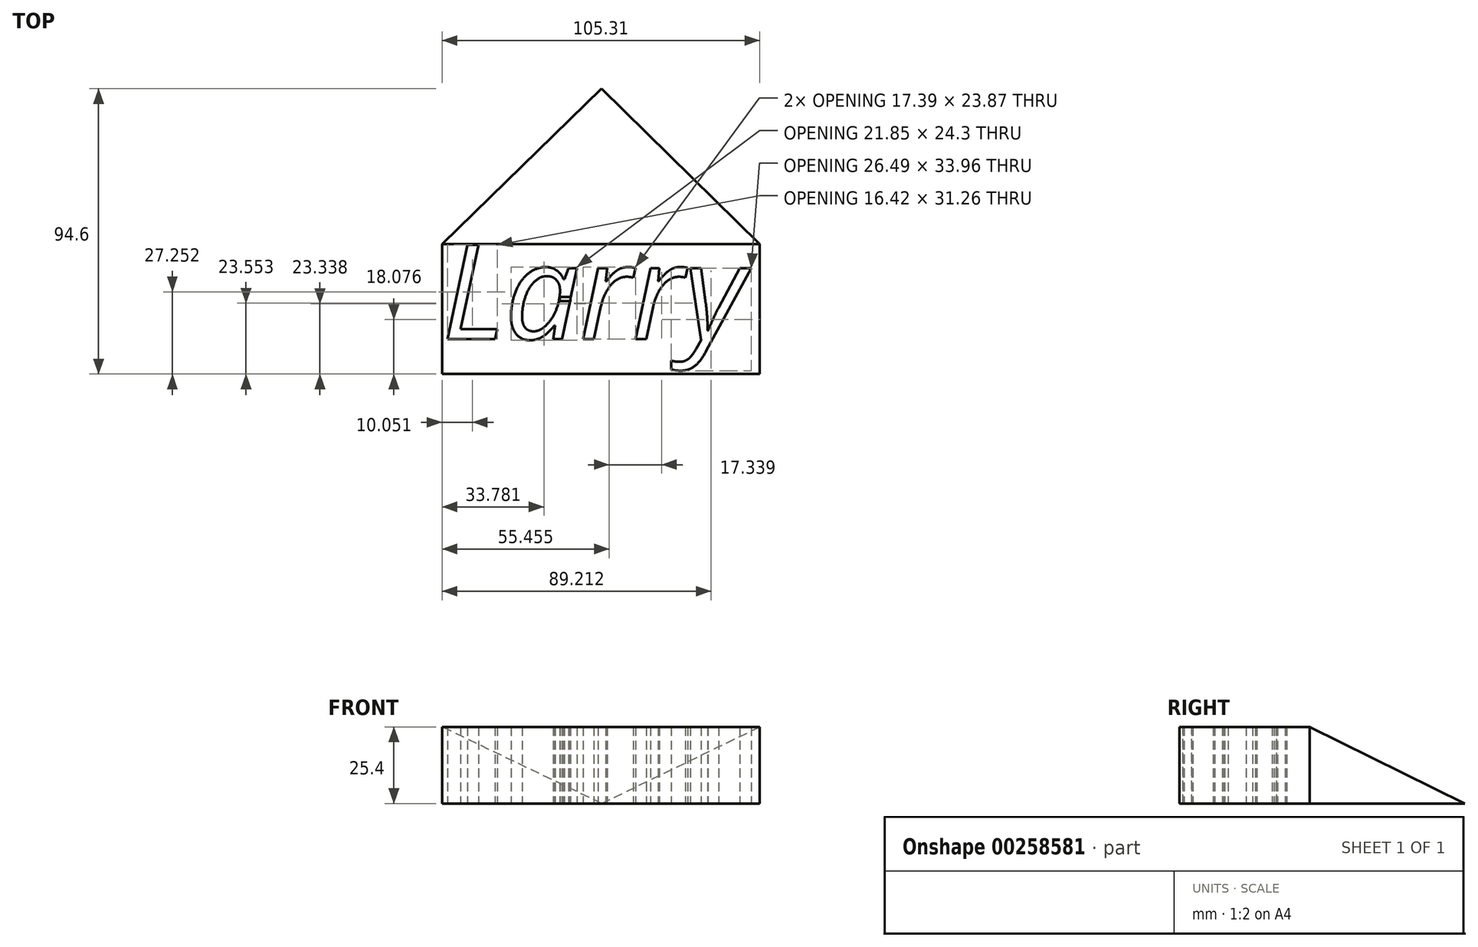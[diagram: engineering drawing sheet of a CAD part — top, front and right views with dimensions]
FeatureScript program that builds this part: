
annotation { "Feature Type Name" : "Feature", "Feature Type Description" : "" }
export const myFeature = defineFeature(function(context is Context, id is Id, definition is map)
    precondition{}
    {
        {
            var Q0;
            Q0=qCreatedBy(makeId("Top.planeOp"),FACE);
            var sketch = newSketch(context, id + "F0", { "sketchPlane" : qUnion([Q0])});
            skText(sketch, "E0", { "text": "Larry", "fontName": "OpenSans-Italic.ttf"});
            skLineSegment(sketch, "E1.bottom", {"start": v(-75.1, 0) * mm, "end": v(30.21, 0) * mm});
            skLineSegment(sketch, "E1.top", {"start": v(-75.1, -43.15) * mm, "end": v(30.21, -43.15) * mm});
            skLineSegment(sketch, "E1.left", {"start": v(-75.1, 0) * mm, "end": v(-75.1, -43.15) * mm});
            skLineSegment(sketch, "E1.right", {"start": v(30.21, 0) * mm, "end": v(30.21, -43.15) * mm});
            skLineSegment(sketch, "E2", {"start": v(-41.85, -28.03) * mm, "end": v(-40.75, -30.14) * mm});
            skLineSegment(sketch, "E3", {"start": v(-40.75, -30.14) * mm, "end": v(-41.85, -28.03) * mm});
            skLineSegment(sketch, "E4", {"start": v(-42.88, -28.56) * mm, "end": v(-42.88, -31.53) * mm});
            skLineSegment(sketch, "E5.bottom", {"start": v(-36.08, -17.57) * mm, "end": v(-32.5, -17.57) * mm});
            skLineSegment(sketch, "E5.top", {"start": v(-36.08, -18.92) * mm, "end": v(-32.5, -18.92) * mm});
            skLineSegment(sketch, "E5.left", {"start": v(-36.08, -17.57) * mm, "end": v(-36.08, -18.92) * mm});
            skLineSegment(sketch, "E5.right", {"start": v(-32.5, -17.57) * mm, "end": v(-32.5, -18.92) * mm});
            const initialGuessF0  = {"E0": [-0.0751, -0.03153, 1, 0, 0.03153]};
            skSetInitialGuess(sketch, initialGuessF0);
            skSolve(sketch);
        }
        {
            var Q0;
            Q0 = qSketchRegion(id + "F0", true);
            var Q1;
            {var subQ6=sQuery(id+"F0.wireOp",EDGE,"E5.bottom");Q1=makeQuery(id+"F0.imprint","IMPRINT",FACE,{"disambiguationData":[TD([[makeQuery(id+"F0.imprint","IMPRINT",EDGE,{"derivedFrom":subQ6}),-1.0]])]});}
            var Q2;
            {var subQ0=sQuery(id+"F0.wireOp",EDGE,"E0.sketch_text.stroke-22");Q2=makeQuery(id+"F0.imprint","IMPRINT",FACE,{"disambiguationData":[TD([[makeQuery(id+"F0.imprint","IMPRINT",EDGE,{"derivedFrom":subQ0}),1.0]])]});}
            extrude(context, id + "F1", {"entities" : qUnion([Q0, Q1, Q2]), "depth" : 25.4 * mm});
        }
        {
            var Q0;
            Q0=qCreatedBy(makeId("Top.planeOp"),FACE);
            var sketch = newSketch(context, id + "F2", { "sketchPlane" : qUnion([Q0])});
            skLineSegment(sketch, "E6", {"start": v(-74.27, 0) * mm, "end": v(29.87, 0) * mm});
            skPoint(sketch, "E7", {"position": v(-22.2, 51.45) * mm});
            skPoint(sketch, "E7.positionSnap0", {"position": v(-22.2, 0) * mm});
            skSolve(sketch);
        }
        {
            var Q1;
            Q1=sQuery(id+"F2.wireOp",VERTEX,"E7");
            var Q2;
            Q2=makeQuery(id+"F1.opExtrude","SWEPT_FACE",FACE,{"disambiguationData":[OSD([sQuery(id+"F0.wireOp",EDGE,"E1.bottom")])]});
            loft(context, id + "F3", {"operationType" : NewBodyOperationType.ADD, "sheetProfilesArray" : [{ "sheetProfileEntities" : qUnion([Q1]) }, { "sheetProfileEntities" : qUnion([Q2]) }]});
        }
    });
